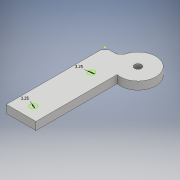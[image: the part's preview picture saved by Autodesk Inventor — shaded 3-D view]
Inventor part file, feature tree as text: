
AUTODESK INVENTOR PART (.ipt)
format: ipt  version: 2018.2 (Build 222227000, 227)  size: 110,080 bytes
history: native  units: mm
features: chamfer x2, sketch x2, extrude x1
ambient origin geometry x8: Origin, YZ Plane, XZ Plane, XY Plane, X Axis, Y Axis, Z Axis, Center Point
bodies: Solid1 (feature_tree)
feature tree (5):
  extrude  "Extrusion1"  Depth=50.0mm
  chamfer  "Chamfer1"  Distance=4.0mm
  chamfer  "Chamfer2"  Distance=2.0mm Angle=45.0deg
  sketch  "Sketch2"  dims[d7=2.0mm d8=2.0mm d9=45.0deg d10=3.25mm d11=3.25mm d12=3.5mm]
  sketch  "Sketch1"  dims[d0=15.0mm d1=50.0mm d2=4.0mm d3=0.0mm d4=2.0mm d5=2.0mm d6=45.0deg]
